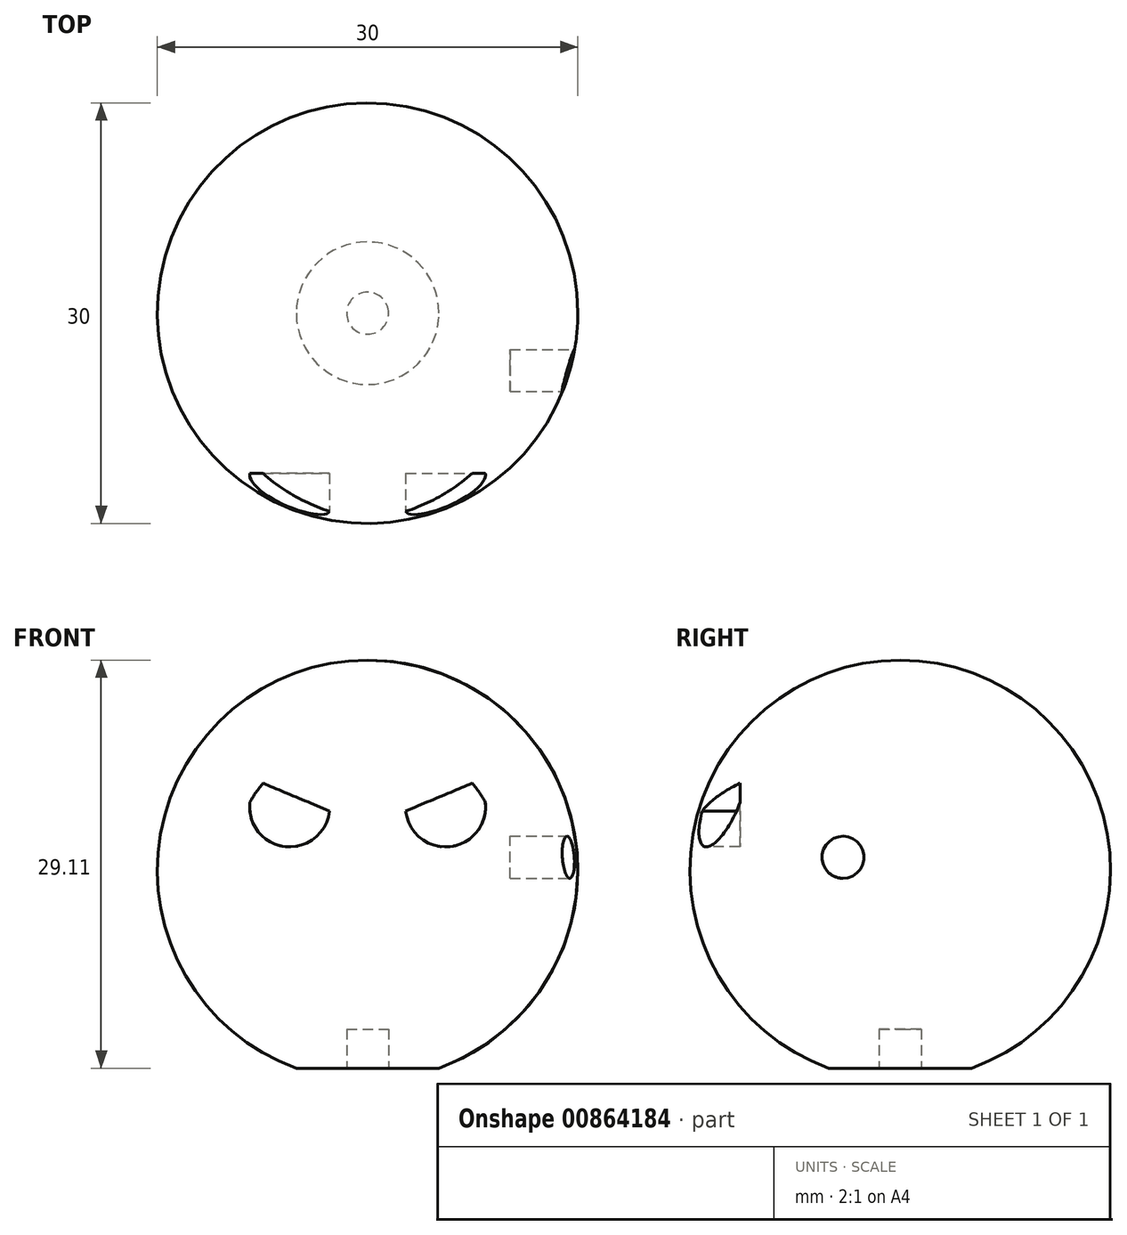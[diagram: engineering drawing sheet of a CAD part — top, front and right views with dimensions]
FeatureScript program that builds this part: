
annotation { "Feature Type Name" : "Feature", "Feature Type Description" : "" }
export const myFeature = defineFeature(function(context is Context, id is Id, definition is map)
    precondition{}
    {
        {
            var Q0;
            Q0=qCreatedBy(makeId("Front.planeOp"),FACE);
            var sketch = newSketch(context, id + "F0", { "sketchPlane" : qUnion([Q0])});
            skLineSegment(sketch, "E0", {"start": v(0, 0) * mm, "end": v(0, 30) * mm});
            skArc(sketch, "E1", {"start": v(0, 0) * mm, "mid": v(15, 15) * mm, "end": v(0, 30) * mm});
            skSolve(sketch);
        }
        {
            var Q0;
            Q0=makeQuery(id+"F0.imprint","IMPRINT",FACE,{"disambiguationData":[TD([[makeQuery(id+"F0.imprint","IMPRINT",EDGE,{"derivedFrom":sQuery(id+"F0.wireOp",EDGE,"E0")}),-1.0]])]});
            var Q1;
            Q1=sQuery(id+"F0.wireOp",EDGE,"E0");
            revolve(context, id + "F1", {"surfaceOperationType" : NewSurfaceOperationType.NEW, "entities" : qUnion([Q0]), "axis" : qUnion([Q1]), "revolveType" : RevolveType.FULL});
        }
        {
            var Q0;
            Q0=qCreatedBy(makeId("Front.planeOp"),FACE);
            cPlane(context, id + "F2", {"entities" : qUnion([Q0]), "cplaneType" : CPlaneType.OFFSET, "offset" : 25.4 * mm, "width" : 152.4 * mm, "height" : 152.4 * mm});
        }
        {
            var Q0;
            Q0=qCreatedBy(makeId("Right.planeOp"),FACE);
            cPlane(context, id + "F3", {"entities" : qUnion([Q0]), "cplaneType" : CPlaneType.OFFSET, "offset" : 25.4 * mm, "width" : 152.4 * mm, "height" : 152.4 * mm});
        }
        {
            var Q0;
            Q0=qCreatedBy(id+"F2.planeOp",FACE);
            var sketch = newSketch(context, id + "F4", { "sketchPlane" : qUnion([Q0])});
            skLineSegment(sketch, "E2", {"start": v(-2.72, 19.24) * mm, "end": v(-7.78, 21.34) * mm});
            skArc(sketch, "E3", {"start": v(-7.78, 21.34) * mm, "mid": v(-6.66, 16.9) * mm, "end": v(-2.72, 19.24) * mm});
            skLineSegment(sketch, "E4.MirrorCS", {"start": v(2.72, 19.24) * mm, "end": v(7.78, 21.34) * mm});
            skArc(sketch, "E5.MirrorCS", {"start": v(7.78, 21.34) * mm, "mid": v(6.66, 16.9) * mm, "end": v(2.72, 19.24) * mm});
            skSolve(sketch);
        }
        {
            var Q0;
            Q0=makeQuery(id+"F4.imprint","IMPRINT",FACE,{"disambiguationData":[TD([[makeQuery(id+"F4.imprint","IMPRINT",EDGE,{"derivedFrom":sQuery(id+"F4.wireOp",EDGE,"E2")}),1.0]])]});
            var Q1;
            Q1=makeQuery(id+"F4.imprint","IMPRINT",FACE,{"disambiguationData":[TD([[makeQuery(id+"F4.imprint","IMPRINT",EDGE,{"derivedFrom":sQuery(id+"F4.wireOp",EDGE,"E4.MirrorCS")}),-1.0]])]});
            extrude(context, id + "F5", {"entities" : qUnion([Q0, Q1]), "operationType" : NewBodyOperationType.REMOVE, "oppositeDirection" : true, "depth" : 13.97 * mm, "offsetDistance" : 25.4 * mm});
        }
        {
            var Q0;
            Q0=qCreatedBy(id+"F3.planeOp",FACE);
            var sketch = newSketch(context, id + "F6", { "sketchPlane" : qUnion([Q0])});
            skCircle(sketch, "E6", {"center": v(-4.09, 15.94) * mm, "radius": 1.5 * mm});
            skSolve(sketch);
        }
        {
            var Q0;
            Q0=makeQuery(id+"F6.imprint","IMPRINT",FACE,{"disambiguationData":[TD([[makeQuery(id+"F6.imprint","IMPRINT",EDGE,{"derivedFrom":sQuery(id+"F6.wireOp",EDGE,"E6")}),1.0]])]});
            extrude(context, id + "F7", {"entities" : qUnion([Q0]), "operationType" : NewBodyOperationType.REMOVE, "oppositeDirection" : true, "depth" : 15.24 * mm, "offsetDistance" : 25.4 * mm});
        }
        {
            var Q0;
            Q0=qCreatedBy(id+"F2.planeOp",FACE);
            var sketch = newSketch(context, id + "F8", { "sketchPlane" : qUnion([Q0])});
            skLineSegment(sketch, "E7.bottom", {"start": v(-16.84, 0.89) * mm, "end": v(19.29, 0.89) * mm});
            skLineSegment(sketch, "E7.top", {"start": v(-16.84, -8.9) * mm, "end": v(19.29, -8.9) * mm});
            skLineSegment(sketch, "E7.left", {"start": v(-16.84, 0.89) * mm, "end": v(-16.84, -8.9) * mm});
            skLineSegment(sketch, "E7.right", {"start": v(19.29, 0.89) * mm, "end": v(19.29, -8.9) * mm});
            skSolve(sketch);
        }
        {
            var Q0;
            Q0=makeQuery(id+"F8.imprint","IMPRINT",FACE,{"disambiguationData":[TD([[makeQuery(id+"F8.imprint","IMPRINT",EDGE,{"derivedFrom":sQuery(id+"F8.wireOp",EDGE,"E7.bottom")}),-1.0]])]});
            extrude(context, id + "F9", {"entities" : qUnion([Q0]), "operationType" : NewBodyOperationType.REMOVE, "oppositeDirection" : true, "depth" : 76.2 * mm, "offsetDistance" : 25.4 * mm});
        }
        {
            var Q0;
            Q0=makeQuery(id+"F9.boolean.opBoolean","COPY",FACE,{"derivedFrom":makeQuery(id+"F9.opExtrude","SWEPT_FACE",FACE,{"disambiguationData":[OSD([sQuery(id+"F8.wireOp",EDGE,"E7.bottom")])]})});
            var sketch = newSketch(context, id + "F10", { "sketchPlane" : qUnion([Q0])});
            skCircle(sketch, "E8", {"center": v(0, 0) * mm, "radius": 1.5 * mm});
            skSolve(sketch);
        }
        {
            var Q0;
            Q0=makeQuery(id+"F10.imprint","IMPRINT",FACE,{"disambiguationData":[TD([[makeQuery(id+"F10.imprint","IMPRINT",EDGE,{"derivedFrom":sQuery(id+"F10.wireOp",EDGE,"E8")}),1.0]])]});
            extrude(context, id + "F11", {"entities" : qUnion([Q0]), "operationType" : NewBodyOperationType.REMOVE, "oppositeDirection" : true, "depth" : 2.8 * mm, "offsetDistance" : 25.4 * mm});
        }
    });
